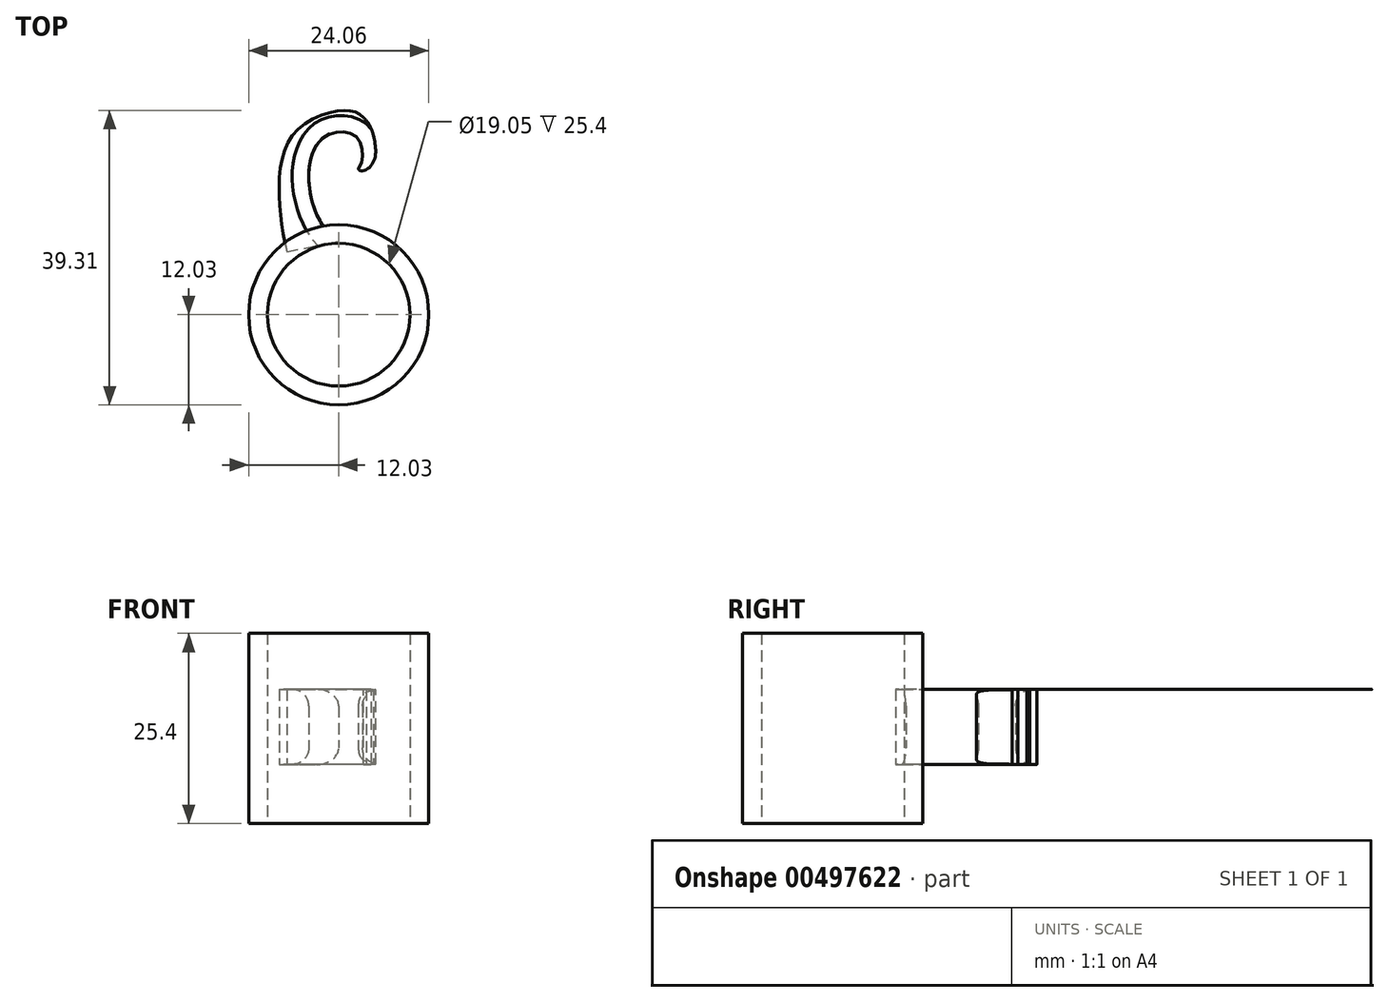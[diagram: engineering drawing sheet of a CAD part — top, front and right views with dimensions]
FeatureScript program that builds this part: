
annotation { "Feature Type Name" : "Feature", "Feature Type Description" : "" }
export const myFeature = defineFeature(function(context is Context, id is Id, definition is map)
    precondition{}
    {
        {
            var Q0;
            Q0=qCreatedBy(makeId("Top.planeOp"),FACE);
            var sketch = newSketch(context, id + "F0", { "sketchPlane" : qUnion([Q0])});
            skCircle(sketch, "E0", {"center": v(0, 0) * mm, "radius": 9.53 * mm});
            skCircle(sketch, "E1", {"center": v(0, 0) * mm, "radius": 12.03 * mm});
            skSolve(sketch);
        }
        {
            var Q0;
            Q0 = qSketchRegion(id + "F0", true);
            extrude(context, id + "F1", {"entities" : qUnion([Q0]), "depth" : 25.4 * mm, "offsetDistance" : 25 * mm});
        }
        {
            var Q0;
            Q0=qCreatedBy(makeId("Top.planeOp"),FACE);
            var sketch = newSketch(context, id + "F2", { "sketchPlane" : qUnion([Q0])});
            skFitSpline(sketch, "E2", {"points": [v(0, 9.79) * mm, v(-4, 18.39) * mm, v(-1.62, 23.94) * mm, v(2.33, 23.76) * mm, v(3.17, 21.24) * mm, v(2.62, 19.46) * mm], "startDerivative": vector(-27.25, 16.68) * mm, "endDerivative": vector(-8.9, -11.19) * mm});
            skFitSpline(sketch, "E3.trimOffspring", {"points": [v(1.71, 19.69) * mm, v(3.42, 19.93) * mm, v(4.62, 23.95) * mm, v(3.3, 26.32) * mm], "startDerivative": vector(4.14, -9.93) * mm, "endDerivative": vector(-3.6, 3.14) * mm});
            skFitSpline(sketch, "E4", {"points": [v(3.69, 25.9) * mm, v(4.62, 23.95) * mm, v(4.5, 20.17) * mm, v(2.62, 19.46) * mm], "startDerivative": vector(4.95, -5.62) * mm, "endDerivative": vector(-3.63, 6.52) * mm});
            skFitSpline(sketch, "E5", {"points": [v(3.31, 26.31) * mm, v(0.8, 27.28) * mm, v(-5.65, 24.57) * mm, v(-7.96, 17.15) * mm, v(-6.92, 8.42) * mm], "startDerivative": vector(-11.77, 11.8) * mm, "endDerivative": vector(6.33, -28.06) * mm});
            skLineSegment(sketch, "E6", {"start": v(-6.92, 8.42) * mm, "end": v(0, 9.79) * mm});
            skSolve(sketch);
        }
        {
            var Q0;
            Q0 = qSketchRegion(id + "F2", true);
            extrude(context, id + "F3", {"entities" : qUnion([Q0]), "depth" : 10 * mm, "offsetDistance" : 25 * mm});
        }
        {
            var Q0;
            Q0=makeQuery(id+"F3.opExtrude","CAP_EDGE",EDGE,{"disambiguationData":[OSD([sQuery(id+"F2.wireOp",EDGE,"E2")])],"isStart":false});
            var Q1;
            Q1=makeQuery(id+"F3.opExtrude","CAP_EDGE",EDGE,{"disambiguationData":[OSD([sQuery(id+"F2.wireOp",EDGE,"E2")])],"isStart":true});
            fillet(context, id + "F4", {"entities" : qUnion([Q0, Q1]), "radius" : 2.2 * mm, "tangentPropagation" : true, "allowEdgeOverflow" : false});
        }
        {
            var Q0;
            Q0=makeQuery(id+"F3.opExtrude","SWEPT_BODY",BODY,{"disambiguationData":[OSD([sQuery(id+"F2.wireOp",EDGE,"E2"),sQuery(id+"F2.wireOp",EDGE,"E3.trimOffspring"),sQuery(id+"F2.wireOp",EDGE,"E4"),sQuery(id+"F2.wireOp",EDGE,"E5"),sQuery(id+"F2.wireOp",EDGE,"E6")])]});
            transform(context, id + "F5", {"entities" : qUnion([Q0]), "transformType" : TransformType.TRANSLATION_3D, "dx" : 0 * mm, "dy" : 0 * mm, "dz" : 7.9 * mm, "makeCopy" : false});
        }
    });
